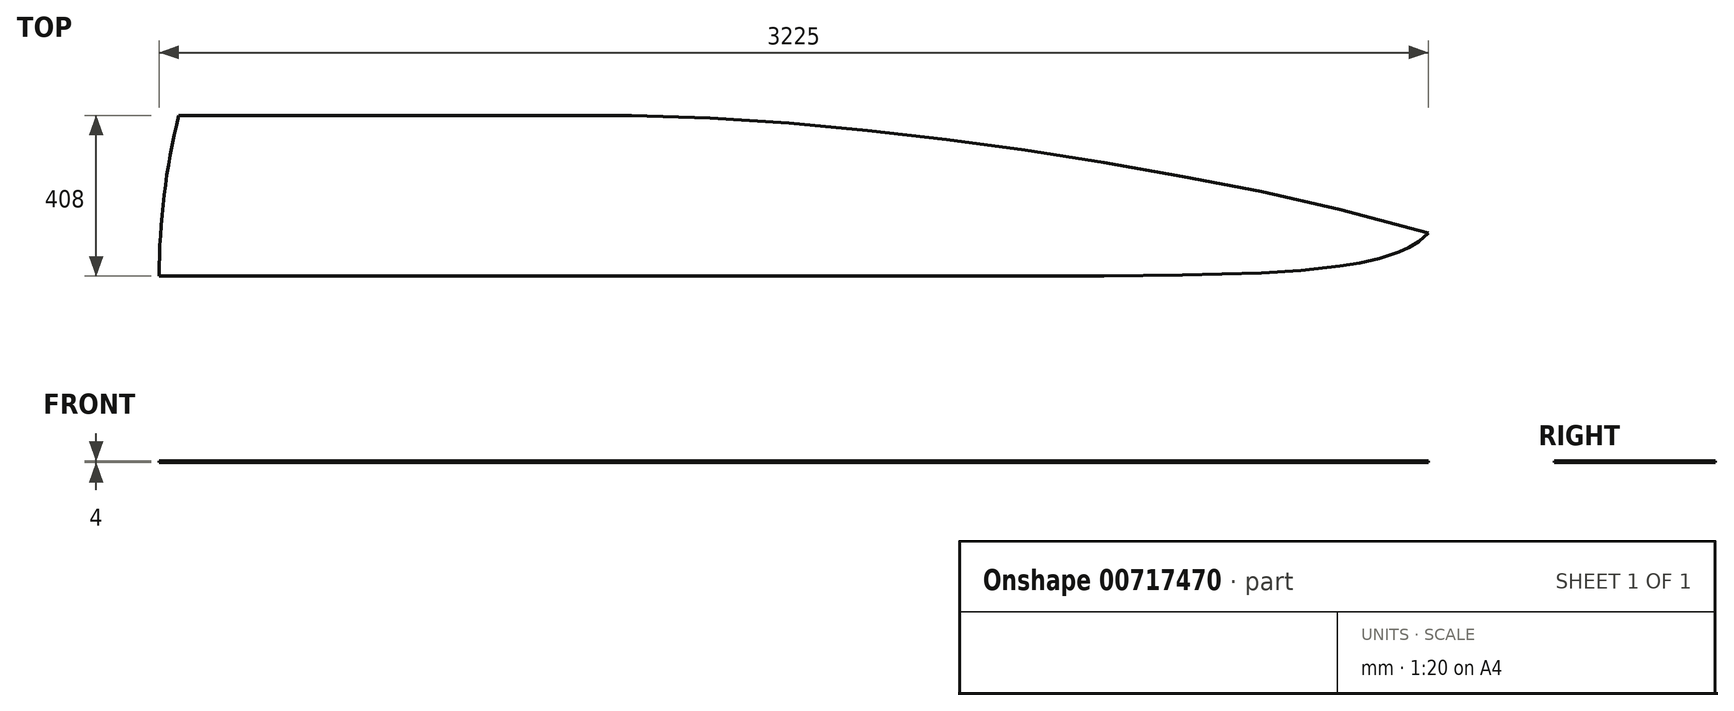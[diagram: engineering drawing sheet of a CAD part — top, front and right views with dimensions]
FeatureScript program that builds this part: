
annotation { "Feature Type Name" : "Feature", "Feature Type Description" : "" }
export const myFeature = defineFeature(function(context is Context, id is Id, definition is map)
    precondition{}
    {
        {
            var Q0;
            Q0=qCreatedBy(makeId("Top.planeOp"),FACE);
            var sketch = newSketch(context, id + "F0", { "sketchPlane" : qUnion([Q0])});
            skLineSegment(sketch, "E0", {"start": v(1575, 76) * mm, "end": v(1725, 76) * mm});
            skArc(sketch, "E1", {"start": v(0, 0) * mm, "mid": v(12.55, 205.53) * mm, "end": v(50, 408) * mm});
            skLineSegment(sketch, "E2", {"start": v(0, 0) * mm, "end": v(2400, 0) * mm});
            skLineSegment(sketch, "E3", {"start": v(50, 408) * mm, "end": v(1000, 408) * mm});
            skLineSegment(sketch, "E4", {"start": v(1000, 408) * mm, "end": v(1000, 0) * mm});
            skLineSegment(sketch, "E5.1.0.0", {"start": v(1200, 407) * mm, "end": v(1200, 0) * mm});
            skLineSegment(sketch, "E5.2.0.0", {"start": v(1400, 401) * mm, "end": v(1400, 0) * mm});
            skLineSegment(sketch, "E5.3.0.0", {"start": v(1600, 388) * mm, "end": v(1600, 0) * mm});
            skLineSegment(sketch, "E5.4.0.0", {"start": v(1800, 370) * mm, "end": v(1800, 0) * mm});
            skLineSegment(sketch, "E5.5.0.0", {"start": v(2000, 347) * mm, "end": v(2000, 0) * mm});
            skLineSegment(sketch, "E5.6.0.0", {"start": v(2200, 320) * mm, "end": v(2200, 0) * mm});
            skLineSegment(sketch, "E5.7.0.0", {"start": v(2400, 288) * mm, "end": v(2400, 0) * mm});
            skLineSegment(sketch, "E5.8.0.0", {"start": v(2600, 253) * mm, "end": v(2600, 0) * mm});
            skLineSegment(sketch, "E5.9.0.0", {"start": v(2800, 214) * mm, "end": v(2800, 0) * mm});
            skLineSegment(sketch, "E5.10.0.0", {"start": v(3000, 169) * mm, "end": v(3000, 0) * mm});
            skLineSegment(sketch, "E5.11.0.0", {"start": v(3200, 116) * mm, "end": v(3200, 0) * mm});
            skLineSegment(sketch, "E5.direction1", {"start": v(1000, 0) * mm, "end": v(1200, 0) * mm, "construction": true});
            skLineSegment(sketch, "E6", {"start": v(3225, 109) * mm, "end": v(3200, 116) * mm});
            skLineSegment(sketch, "E7", {"start": v(3000, 169) * mm, "end": v(2800, 214) * mm});
            skLineSegment(sketch, "E8", {"start": v(2600, 253) * mm, "end": v(2800, 214) * mm});
            skLineSegment(sketch, "E9", {"start": v(3000, 169) * mm, "end": v(3200, 116) * mm});
            skLineSegment(sketch, "E10", {"start": v(1000, 408) * mm, "end": v(1200, 407) * mm});
            skLineSegment(sketch, "E11", {"start": v(1400, 401) * mm, "end": v(1200, 407) * mm});
            skLineSegment(sketch, "E12", {"start": v(1400, 401) * mm, "end": v(1600, 388) * mm});
            skLineSegment(sketch, "E13", {"start": v(1600, 388) * mm, "end": v(1800, 370) * mm});
            skLineSegment(sketch, "E14", {"start": v(1800, 370) * mm, "end": v(2000, 347) * mm});
            skLineSegment(sketch, "E15", {"start": v(2000, 347) * mm, "end": v(2200, 320) * mm});
            skLineSegment(sketch, "E16", {"start": v(2200, 320) * mm, "end": v(2400, 288) * mm});
            skLineSegment(sketch, "E17", {"start": v(2400, 288) * mm, "end": v(2600, 253) * mm});
            skLineSegment(sketch, "E18", {"start": v(2600, 2) * mm, "end": v(2400, 0) * mm});
            skLineSegment(sketch, "E19", {"start": v(2600, 2) * mm, "end": v(2800, 8) * mm});
            skLineSegment(sketch, "E20", {"start": v(2900, 0) * mm, "end": v(2900, 14) * mm});
            skLineSegment(sketch, "E21", {"start": v(2900, 14) * mm, "end": v(3000, 25) * mm});
            skLineSegment(sketch, "E22", {"start": v(2800, 8) * mm, "end": v(2900, 14) * mm});
            skLineSegment(sketch, "E23", {"start": v(3100, 0) * mm, "end": v(3100, 44) * mm});
            skLineSegment(sketch, "E24", {"start": v(3050, 33) * mm, "end": v(3050, 0) * mm});
            skLineSegment(sketch, "E25", {"start": v(3150, 61) * mm, "end": v(3150, 0) * mm});
            skLineSegment(sketch, "E26", {"start": v(3050, 33) * mm, "end": v(3100, 44) * mm});
            skLineSegment(sketch, "E27", {"start": v(3000, 25) * mm, "end": v(3050, 33) * mm});
            skLineSegment(sketch, "E28", {"start": v(3100, 44) * mm, "end": v(3150, 61) * mm});
            skLineSegment(sketch, "E29", {"start": v(3175, 0) * mm, "end": v(3175, 72) * mm});
            skLineSegment(sketch, "E30", {"start": v(3150, 61) * mm, "end": v(3175, 72) * mm});
            skLineSegment(sketch, "E31", {"start": v(3175, 72) * mm, "end": v(3200, 87) * mm});
            skLineSegment(sketch, "E32", {"start": v(3200, 87) * mm, "end": v(3225, 109) * mm});
            skSolve(sketch);
        }
        {
            var Q0;
            Q0 = qSketchRegion(id + "F0", true);
            extrude(context, id + "F1", {"entities" : qUnion([Q0]), "depth" : 4 * mm, "offsetDistance" : 25 * mm});
        }
    });
